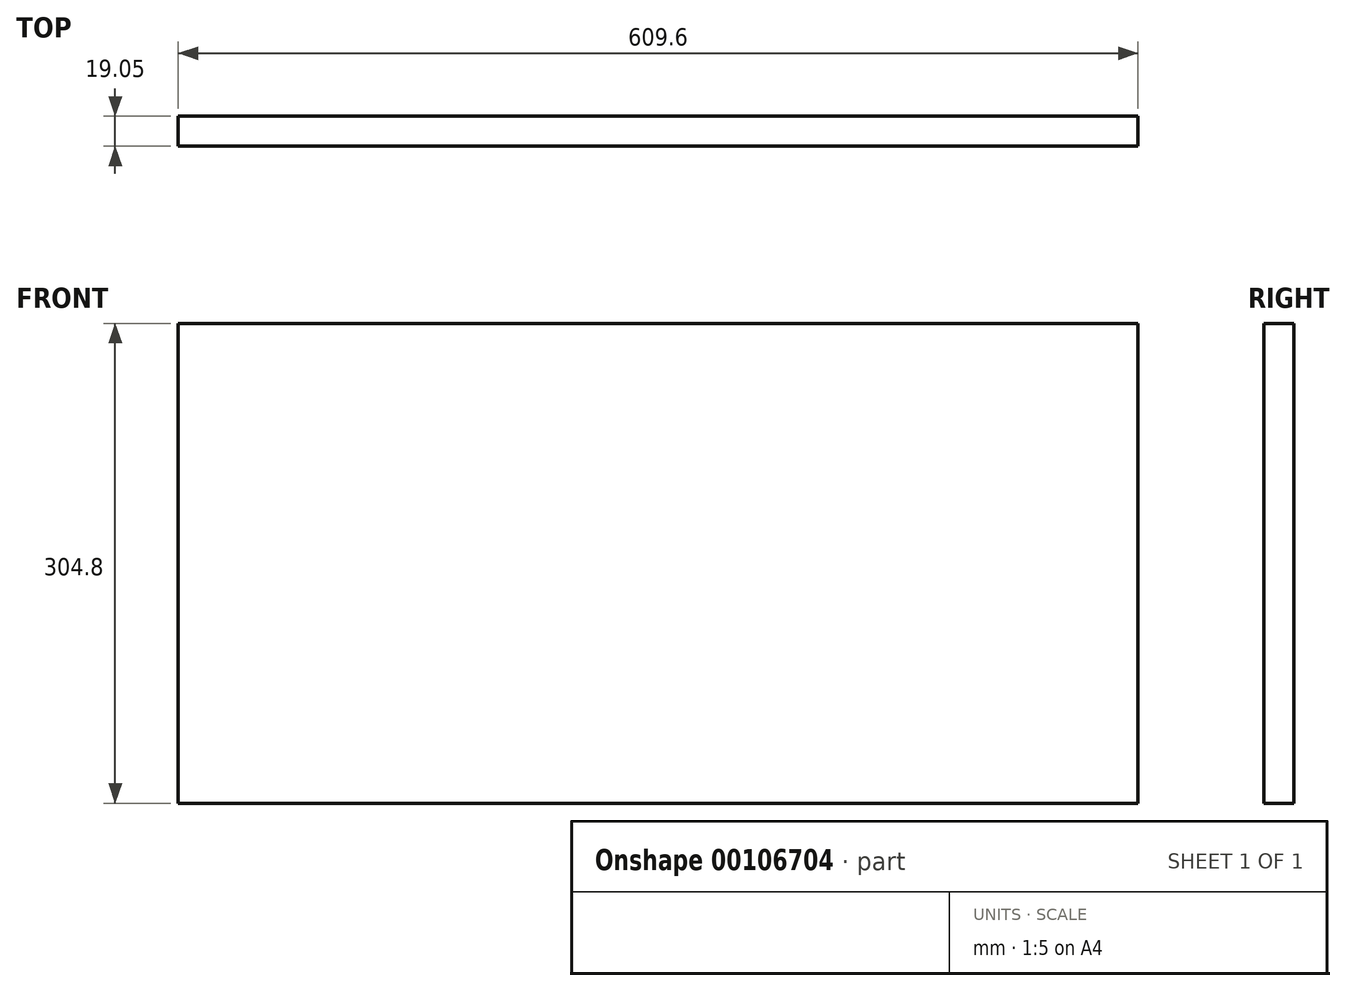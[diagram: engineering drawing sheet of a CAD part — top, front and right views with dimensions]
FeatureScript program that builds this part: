
annotation { "Feature Type Name" : "Feature", "Feature Type Description" : "" }
export const myFeature = defineFeature(function(context is Context, id is Id, definition is map)
    precondition{}
    {
        {
            var Q0;
            Q0=qCreatedBy(makeId("Front.planeOp"),FACE);
            var sketch = newSketch(context, id + "F0", { "sketchPlane" : qUnion([Q0])});
            skLineSegment(sketch, "E0.bottom", {"start": v(0, 0) * mm, "end": v(609.6, 0) * mm});
            skLineSegment(sketch, "E0.top", {"start": v(0, 304.8) * mm, "end": v(609.6, 304.8) * mm});
            skLineSegment(sketch, "E0.left", {"start": v(0, 0) * mm, "end": v(0, 304.8) * mm});
            skLineSegment(sketch, "E0.right", {"start": v(609.6, 0) * mm, "end": v(609.6, 304.8) * mm});
            skSolve(sketch);
        }
        {
            var Q0;
            Q0=makeQuery(id+"F0.imprint","IMPRINT",FACE,{"disambiguationData":[TD([[makeQuery(id+"F0.imprint","IMPRINT",EDGE,{"derivedFrom":sQuery(id+"F0.wireOp",EDGE,"E0.bottom")}),1.0]])]});
            extrude(context, id + "F1", {"entities" : qUnion([Q0]), "depth" : 19.05 * mm});
        }
    });
